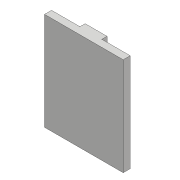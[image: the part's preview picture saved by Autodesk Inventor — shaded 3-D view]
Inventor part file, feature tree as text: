
AUTODESK INVENTOR PART (.ipt)
format: ipt  version: 2018 (Build 220112000, 112)  size: 84,480 bytes
history: native  units: mm
features: extrude x2, sketch x2
ambient origin geometry x8: Origin, YZ Plane, XZ Plane, XY Plane, X Axis, Y Axis, Z Axis, Center Point
bodies: Solid1 (feature_tree)
feature tree (4):
  extrude  "Extrusion1"  Depth=45.0mm
  extrude  "Extrusion2"  Depth=12.5mm
  sketch  "Sketch1"  dims[d0=56.0mm d1=45.0mm]
  sketch  "Sketch2"  dims[d2=4.0mm d3=0.0mm d4=12.5mm d5=10.0mm d6=3.0mm d7=0.0mm]
